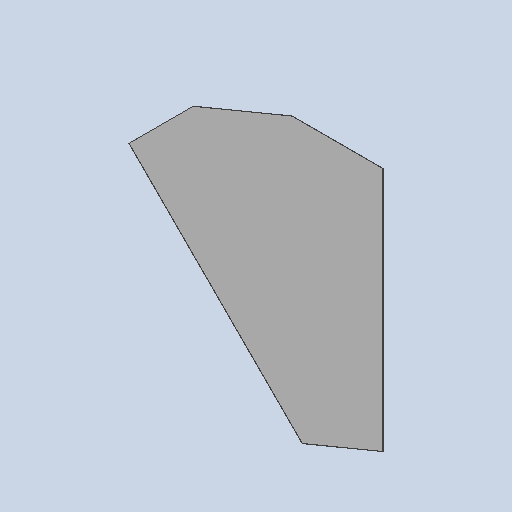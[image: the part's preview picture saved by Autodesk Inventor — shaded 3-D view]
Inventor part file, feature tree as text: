
AUTODESK INVENTOR PART (.ipt)
format: ipt  version: 2025 (Build 290162010, 162A)  size: 129,536 bytes
history: native  units: mm
features: extrude x2, sketch x2, pattern_linear x1
ambient origin geometry x8: Origin, YZ Plane, XZ Plane, XY Plane, X Axis, Y Axis, Z Axis, Center Point
bodies: Solid1 (feature_tree)
feature tree (5):
  extrude  "Extrusion1"  Depth=260.0mm
  extrude  "Extrusion5"  Depth=0.5mm TaperAngle=0.0deg
  pattern_linear  "Rectangular Pattern1"  Spacing1=15.0mm  [1 undecoded]
  sketch  "Sketch1"  dims[d0=513.0mm d2=260.0mm]
  sketch  "Sketch7"  dims[d3=635.0mm d5=0.5mm d6=0.0mm d10=15.0mm d54=8.0mm d55=8.0mm d56=5.0mm d57=5.0mm d58=0.0mm d59=0.0mm d60=300.0mm d62=25.0mm d63=300.0mm d65=25.0mm]
note: 1 required parameter value undecoded (feature->parameter linkage not recoverable at this tier; creation-order binding heuristic only, values carry confidence <= 0.55)
